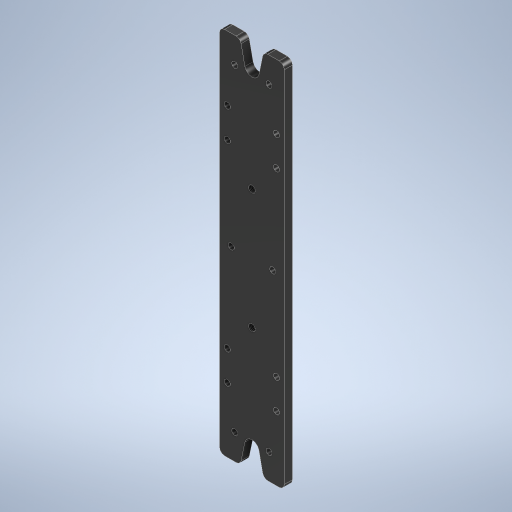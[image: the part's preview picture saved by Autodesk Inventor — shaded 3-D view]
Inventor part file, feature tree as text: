
AUTODESK INVENTOR PART (.ipt)
format: ipt  version: 2024.2 (Build 282272000, 272)  size: 312,320 bytes
history: native  units: mm
features: sketch x1, extrude x1, hole x1
ambient origin geometry x8: Origin, YZ Plane, XZ Plane, XY Plane, X Axis, Y Axis, Z Axis, Center Point
bodies: Solid1 (feature_tree)
feature tree (3):
  sketch  "Sketch1"  dims[d0=63.25mm d1=360.0mm d2=40.5mm d3=176.0mm d4=29.0mm d5=48.0mm d6=33.5mm d7=310.0mm d8=30.0mm d9=37.5mm d10=14.0mm d11=320.0mm d12=8.0mm d13=0.0mm d14=6.0mm d15=6.0mm d16=4.0mm d17=2.0mm d18=90.0deg d19=8.0mm d20=20.594885mm d21=117.0mm d22=6.647mm d23=16.0mm d24=4.0mm d25=2.0mm d26=90.0deg d27=8.0mm d28=20.594885mm d29=5.0mm]
  extrude  "Extrusion1"  Depth=360.0mm
  hole  "Phi6-H7"  [1 undecoded]
note: 1 required parameter value undecoded (feature->parameter linkage not recoverable at this tier; creation-order binding heuristic only, values carry confidence <= 0.55)
